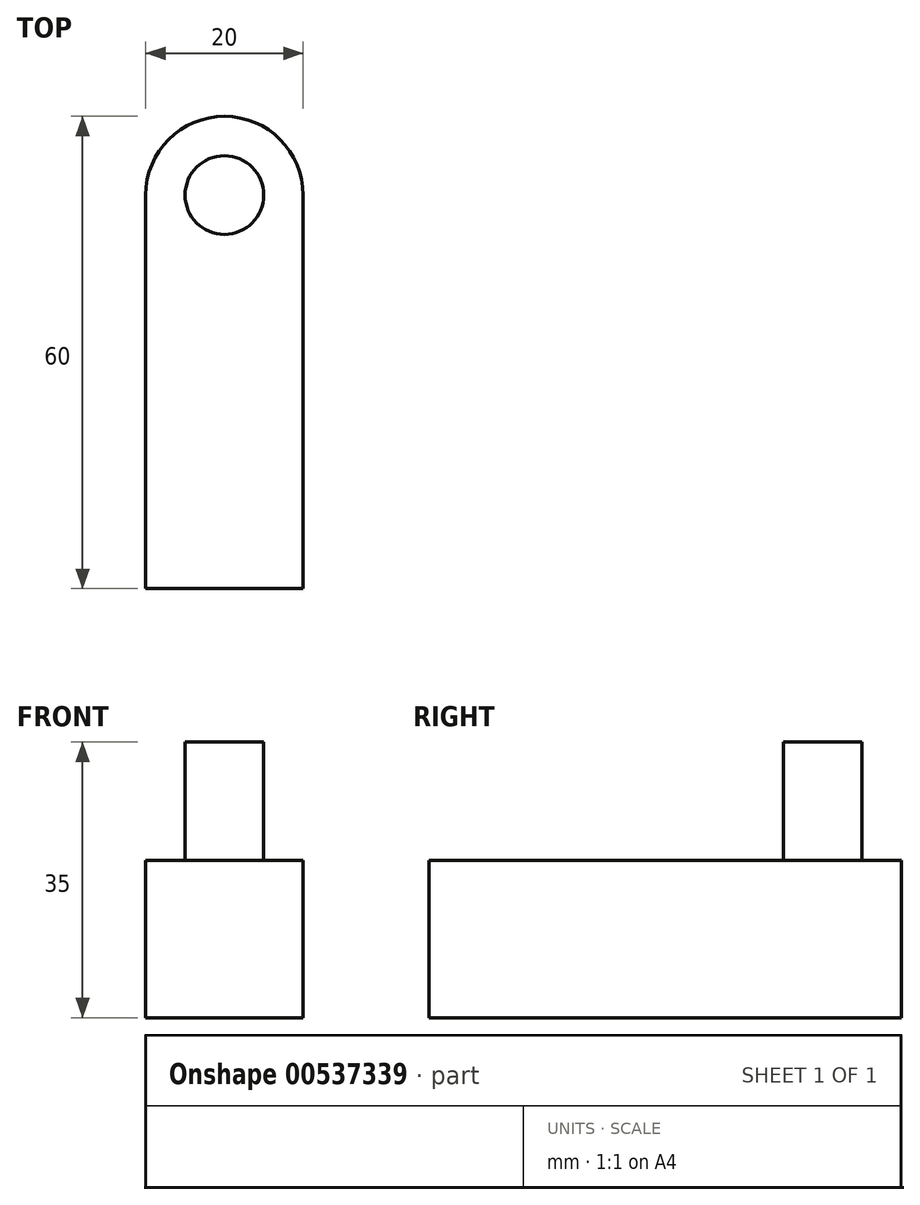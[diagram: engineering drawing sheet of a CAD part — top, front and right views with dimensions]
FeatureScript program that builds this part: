
annotation { "Feature Type Name" : "Feature", "Feature Type Description" : "" }
export const myFeature = defineFeature(function(context is Context, id is Id, definition is map)
    precondition{}
    {
        {
            var Q0;
            Q0=qCreatedBy(makeId("Top.planeOp"),FACE);
            var sketch = newSketch(context, id + "F0", { "sketchPlane" : qUnion([Q0])});
            skLineSegment(sketch, "E0.top", {"start": v(10, -25) * mm, "end": v(-10, -25) * mm});
            skLineSegment(sketch, "E0.left", {"start": v(10, 25) * mm, "end": v(10, -25) * mm});
            skLineSegment(sketch, "E0.right", {"start": v(-10, 25) * mm, "end": v(-10, -25) * mm});
            skPoint(sketch, "E0.middle", {"position": v(0, 0) * mm});
            skArc(sketch, "E1", {"start": v(10, 25) * mm, "mid": v(0, 35) * mm, "end": v(-10, 25) * mm});
            skCircle(sketch, "E2", {"center": v(0, 25) * mm, "radius": 5 * mm});
            skSolve(sketch);
        }
        {
            var Q0;
            Q0=qSketchRegion(id+"F0",true);
            extrude(context, id + "F1", {"entities" : qUnion([Q0]), "endBound" : BoundingType.SYMMETRIC, "depth" : 20 * mm});
        }
        {
            var Q0;
            Q0=qCreatedBy(makeId("Top.planeOp"),FACE);
            var sketch = newSketch(context, id + "F2", { "sketchPlane" : qUnion([Q0])});
            skCircle(sketch, "E3", {"center": v(0, 25) * mm, "radius": 5 * mm});
            skSolve(sketch);
        }
        {
            var Q0;
            Q0=makeQuery(id+"F2.imprint","IMPRINT",FACE,{"disambiguationData":[TD([[makeQuery(id+"F2.imprint","IMPRINT",EDGE,{"derivedFrom":sQuery(id+"F2.wireOp",EDGE,"E3")}),1.0]])]});
            extrude(context, id + "F3", {"entities" : qUnion([Q0]), "operationType" : NewBodyOperationType.ADD, "endBound" : BoundingType.SYMMETRIC, "depth" : 50 * mm});
        }
        {
            var Q0;
            Q0=makeQuery(id+"F3.opExtrude","CAP_FACE",FACE,{"disambiguationData":[OSD([sQuery(id+"F2.wireOp",EDGE,"E3")])],"isStart":true});
            extrude(context, id + "F4", {"entities" : qUnion([Q0]), "operationType" : NewBodyOperationType.REMOVE, "oppositeDirection" : true, "depth" : 15 * mm});
        }
    });
